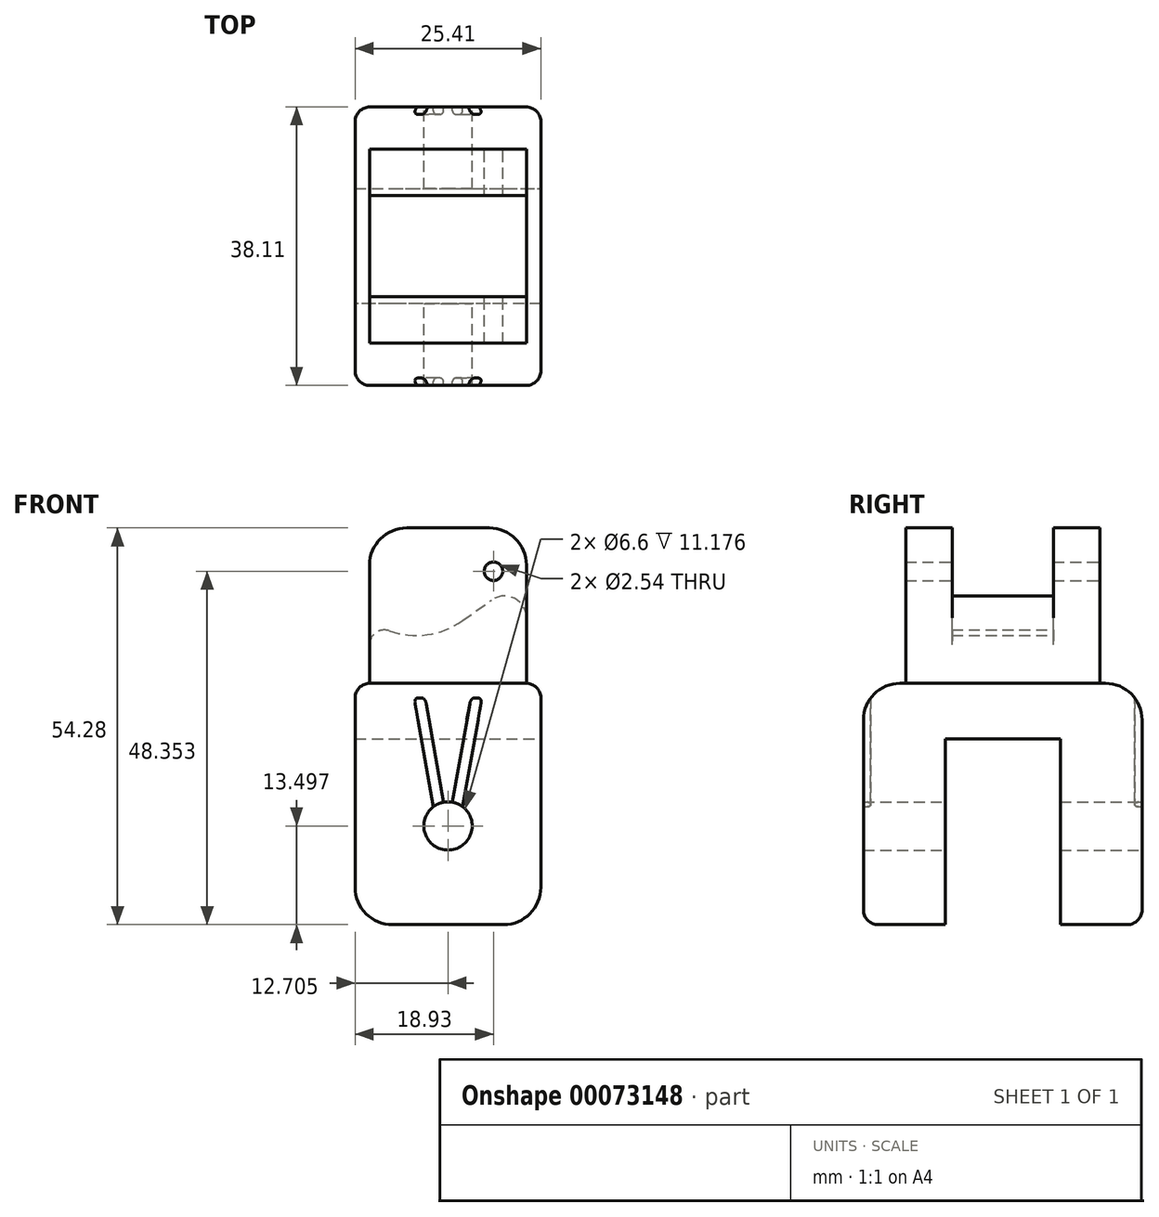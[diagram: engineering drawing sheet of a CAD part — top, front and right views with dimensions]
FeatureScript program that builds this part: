
annotation { "Feature Type Name" : "Feature", "Feature Type Description" : "" }
export const myFeature = defineFeature(function(context is Context, id is Id, definition is map)
    precondition{}
    {
        {
            var Q0;
            Q0=qCreatedBy(makeId("Front.planeOp"),FACE);
            var sketch = newSketch(context, id + "F0", { "sketchPlane" : qUnion([Q0])});
            skLineSegment(sketch, "E0.rect.bottom", {"start": v(6.35, -4.28) * mm, "end": v(-6.35, -4.28) * mm});
            skLineSegment(sketch, "E0.rect.left", {"start": v(6.35, -4.28) * mm, "end": v(6.35, 4.28) * mm});
            skLineSegment(sketch, "E0.rect.right", {"start": v(-6.35, -4.28) * mm, "end": v(-6.35, 4.28) * mm});
            skPoint(sketch, "E0.rect.middle", {"position": v(0, 0) * mm});
            skArc(sketch, "E1", {"start": v(-6.35, 4.28) * mm, "mid": v(0, 2.26) * mm, "end": v(6.35, 4.28) * mm});
            skLineSegment(sketch, "E2", {"start": v(6.35, 4.28) * mm, "end": v(15.1, 10.47) * mm});
            skLineSegment(sketch, "E3", {"start": v(15.1, 10.47) * mm, "end": v(15.1, -4.28) * mm});
            skLineSegment(sketch, "E4", {"start": v(15.1, -4.28) * mm, "end": v(6.35, -4.28) * mm});
            skSolve(sketch);
        }
        {
            var Q0;
            Q0=makeQuery(id+"F0.imprint","IMPRINT",FACE,{"disambiguationData":[TD([[makeQuery(id+"F0.imprint","IMPRINT",EDGE,{"derivedFrom":sQuery(id+"F0.wireOp",EDGE,"E0.rect.bottom")}),-1.0]])]});
            var Q1;
            Q1=makeQuery(id+"F0.imprint","IMPRINT",FACE,{"disambiguationData":[TD([[makeQuery(id+"F0.imprint","IMPRINT",EDGE,{"derivedFrom":sQuery(id+"F0.wireOp",EDGE,"E0.rect.left")}),-1.0]])]});
            extrude(context, id + "F1", {"entities" : qUnion([Q0, Q1]), "depth" : 13.85 * mm});
        }
        {
            var Q0;
            Q0=makeQuery(id+"F1.opExtrude","SWEPT_EDGE",EDGE,{"disambiguationData":[OSD([sQuery(id+"F0.wireOp",EDGE,"E0.rect.right"),sQuery(id+"F0.wireOp",EDGE,"E1")])]});
            fillet(context, id + "F2", {"entities" : qUnion([Q0]), "radius" : 2 * mm, "tangentPropagation" : true, "allowEdgeOverflow" : false});
        }
        {
            var Q0;
            Q0=makeQuery(id+"F1.opExtrude","CAP_FACE",FACE,{"disambiguationData":[OSD([sQuery(id+"F0.wireOp",EDGE,"E0.rect.bottom"),sQuery(id+"F0.wireOp",EDGE,"E0.rect.top"),sQuery(id+"F0.wireOp",EDGE,"E0.rect.left"),sQuery(id+"F0.wireOp",EDGE,"E0.rect.right")])],"isStart":false});
            var sketch = newSketch(context, id + "F3", { "sketchPlane" : qUnion([Q0])});
            skLineSegment(sketch, "E5.bottom", {"start": v(-6.35, -4.28) * mm, "end": v(15.1, -4.28) * mm});
            skLineSegment(sketch, "E5.top", {"start": v(-6.35, 16.98) * mm, "end": v(15.1, 16.98) * mm});
            skLineSegment(sketch, "E5.left", {"start": v(-6.35, -4.28) * mm, "end": v(-6.35, 16.98) * mm});
            skLineSegment(sketch, "E5.right", {"start": v(15.1, -4.28) * mm, "end": v(15.1, 16.98) * mm});
            skSolve(sketch);
        }
        {
            var Q0;
            Q0=qSketchRegion(id+"F3",true);
            extrude(context, id + "F4", {"entities" : qUnion([Q0]), "operationType" : NewBodyOperationType.ADD, "depth" : 6.35 * mm});
        }
        {
            var Q0;
            Q0=makeQuery(id+"F1.opExtrude","CAP_FACE",FACE,{"disambiguationData":[OSD([sQuery(id+"F0.wireOp",EDGE,"E0.rect.bottom"),sQuery(id+"F0.wireOp",EDGE,"E0.rect.top"),sQuery(id+"F0.wireOp",EDGE,"E0.rect.left"),sQuery(id+"F0.wireOp",EDGE,"E0.rect.right")])],"isStart":true});
            var sketch = newSketch(context, id + "F5", { "sketchPlane" : qUnion([Q0])});
            skLineSegment(sketch, "E6.bottom", {"start": v(6.35, -4.28) * mm, "end": v(-15.1, -4.28) * mm});
            skLineSegment(sketch, "E6.top", {"start": v(6.35, 16.98) * mm, "end": v(-15.1, 16.98) * mm});
            skLineSegment(sketch, "E6.left", {"start": v(6.35, -4.28) * mm, "end": v(6.35, 16.98) * mm});
            skLineSegment(sketch, "E6.right", {"start": v(-15.1, -4.28) * mm, "end": v(-15.1, 16.98) * mm});
            skSolve(sketch);
        }
        {
            var Q0;
            Q0=qSketchRegion(id+"F5",true);
            extrude(context, id + "F6", {"entities" : qUnion([Q0]), "operationType" : NewBodyOperationType.ADD, "depth" : 6.35 * mm});
        }
        {
            var Q0;
            Q0=makeQuery(id+"F6.opExtrude","CAP_FACE",FACE,{"disambiguationData":[OSD([sQuery(id+"F5.wireOp",EDGE,"E6.bottom"),sQuery(id+"F5.wireOp",EDGE,"E6.top"),sQuery(id+"F5.wireOp",EDGE,"E6.left"),sQuery(id+"F5.wireOp",EDGE,"E6.right")])],"isStart":false});
            var sketch = newSketch(context, id + "F7", { "sketchPlane" : qUnion([Q0])});
            skCircle(sketch, "E7", {"center": v(-10.6, 11.05) * mm, "radius": 1.27 * mm});
            skSolve(sketch);
        }
        {
            var Q0;
            Q0=qSketchRegion(id+"F7",true);
            extrude(context, id + "F8", {"entities" : qUnion([Q0]), "operationType" : NewBodyOperationType.REMOVE, "endBound" : BoundingType.THROUGH_ALL, "oppositeDirection" : true, "depth" : 25.4 * mm});
        }
        {
            var Q0;
            Q0=makeQuery(id+"F6.boolean.opBoolean","MERGE",FACE,{"derivedFrom":[makeQuery(id+"F4.boolean.opBoolean","MERGE",FACE,{"derivedFrom":[makeQuery(id+"F1.opExtrude","SWEPT_FACE",FACE,{"disambiguationData":[OSD([sQuery(id+"F0.wireOp",EDGE,"E0.rect.bottom")])]}),makeQuery(id+"F4.opExtrude","SWEPT_FACE",FACE,{"disambiguationData":[OSD([sQuery(id+"F3.wireOp",EDGE,"E5.bottom")])]})]}),makeQuery(id+"F6.opExtrude","SWEPT_FACE",FACE,{"disambiguationData":[OSD([sQuery(id+"F5.wireOp",EDGE,"E6.bottom")])]})]});
            var sketch = newSketch(context, id + "F9", { "sketchPlane" : qUnion([Q0])});
            skLineSegment(sketch, "E8", {"start": v(15.1, -6.35) * mm, "end": v(-6.35, 20.2) * mm});
            skLineSegment(sketch, "E9", {"start": v(-6.35, -6.35) * mm, "end": v(15.1, 20.2) * mm});
            skLineSegment(sketch, "E10.rect.bottom", {"start": v(17.07, 25.97) * mm, "end": v(-8.33, 25.97) * mm});
            skLineSegment(sketch, "E10.rect.top", {"start": v(17.07, -12.13) * mm, "end": v(-8.32, -12.13) * mm});
            skLineSegment(sketch, "E10.rect.left", {"start": v(17.07, 25.97) * mm, "end": v(17.07, -12.13) * mm});
            skLineSegment(sketch, "E10.rect.right", {"start": v(-8.33, 25.98) * mm, "end": v(-8.33, -12.13) * mm});
            skPoint(sketch, "E10.rect.middle", {"position": v(4.37, 6.92) * mm});
            skSolve(sketch);
        }
        {
            var Q0;
            Q0=qSketchRegion(id+"F9",true);
            extrude(context, id + "F10", {"entities" : qUnion([Q0]), "operationType" : NewBodyOperationType.ADD, "depth" : 7.62 * mm});
        }
        {
            var Q0;
            Q0=makeQuery(id+"F10.opExtrude","CAP_FACE",FACE,{"disambiguationData":[OSD([sQuery(id+"F9.wireOp",EDGE,"E10.rect.bottom"),sQuery(id+"F9.wireOp",EDGE,"E10.rect.top"),sQuery(id+"F9.wireOp",EDGE,"E10.rect.left"),sQuery(id+"F9.wireOp",EDGE,"E10.rect.right")])],"isStart":false});
            var sketch = newSketch(context, id + "F11", { "sketchPlane" : qUnion([Q0])});
            skLineSegment(sketch, "E11.top", {"start": v(17.07, 14.8) * mm, "end": v(-8.33, 14.8) * mm});
            skLineSegment(sketch, "E12", {"start": v(-8.33, -0.95) * mm, "end": v(17.07, -0.95) * mm});
            skSolve(sketch);
        }
        {
            var Q0;
            {var subQ0=sQuery(id+"F11.wireOp",EDGE,"E12");Q0=makeQuery(id+"F11.imprint","IMPRINT",FACE,{"disambiguationData":[TD([[makeQuery(id+"F11.imprint","IMPRINT",EDGE,{"derivedFrom":subQ0}),-1.0]])]});}
            var Q1;
            {var subQ5=makeQuery(id+"F10.opExtrude","CAP_EDGE",EDGE,{"disambiguationData":[OSD([sQuery(id+"F9.wireOp",EDGE,"E10.rect.bottom")])],"isStart":false});Q1=makeQuery(id+"F11.imprint","IMPRINT",FACE,{"disambiguationData":[TD([[makeQuery(id+"F11.imprint","IMPRINT",EDGE,{"derivedFrom":subQ5}),1.0]])]});}
            extrude(context, id + "F12", {"entities" : qUnion([Q0, Q1]), "operationType" : NewBodyOperationType.ADD, "depth" : 25.4 * mm});
        }
        {
            var Q0;
            {var subQ0=sQuery(id+"F9.wireOp",EDGE,"E10.rect.top");Q0=makeQuery(id+"F12.boolean.opBoolean","MERGE",FACE,{"derivedFrom":[makeQuery(id+"F10.opExtrude","SWEPT_FACE",FACE,{"disambiguationData":[OSD([subQ0])]}),makeQuery(id+"F12.opExtrude","SWEPT_FACE",FACE,{"disambiguationData":[OSD([subQ0])]})]});}
            var sketch = newSketch(context, id + "F13", { "sketchPlane" : qUnion([Q0])});
            skCircle(sketch, "E13", {"center": v(-4.38, -23.8) * mm, "radius": 3.3 * mm});
            skSolve(sketch);
        }
        {
            var Q0;
            Q0=qSketchRegion(id+"F13",true);
            extrude(context, id + "F14", {"entities" : qUnion([Q0]), "operationType" : NewBodyOperationType.REMOVE, "endBound" : BoundingType.THROUGH_ALL, "oppositeDirection" : true, "depth" : 25.4 * mm});
        }
        {
            var Q0;
            {var subQ0=sQuery(id+"F9.wireOp",EDGE,"E10.rect.right");var subQ1=makeQuery(id+"F10.opExtrude","CAP_EDGE",EDGE,{"disambiguationData":[OSD([subQ0])],"isStart":false});Q0=makeQuery(id+"F12.opExtrude","CAP_EDGE",EDGE,{"disambiguationData":[OSD([subQ0]),TDD([makeQuery(id+"F11.imprint","IMPRINT",EDGE,{"disambiguationData":[TD([[makeQuery(id+"F11.imprint","INTERSECT",VERTEX,{"derivedFrom":[makeQuery(id+"F10.opExtrude","CAP_EDGE",EDGE,{"disambiguationData":[OSD([sQuery(id+"F9.wireOp",EDGE,"E10.rect.top")])],"isStart":false}),subQ1]}),1.0]])],"derivedFrom":subQ1})])],"isStart":false});}
            var Q1;
            {var subQ0=sQuery(id+"F9.wireOp",EDGE,"E10.rect.left");var subQ1=makeQuery(id+"F10.opExtrude","CAP_EDGE",EDGE,{"disambiguationData":[OSD([subQ0])],"isStart":false});Q1=makeQuery(id+"F12.opExtrude","CAP_EDGE",EDGE,{"disambiguationData":[OSD([subQ0]),TDD([makeQuery(id+"F11.imprint","IMPRINT",EDGE,{"disambiguationData":[TD([[makeQuery(id+"F11.imprint","INTERSECT",VERTEX,{"derivedFrom":[makeQuery(id+"F10.opExtrude","CAP_EDGE",EDGE,{"disambiguationData":[OSD([sQuery(id+"F9.wireOp",EDGE,"E10.rect.top")])],"isStart":false}),subQ1]}),1.0]])],"derivedFrom":subQ1})])],"isStart":false});}
            var Q2;
            {var subQ0=sQuery(id+"F9.wireOp",EDGE,"E10.rect.right");var subQ1=makeQuery(id+"F10.opExtrude","CAP_EDGE",EDGE,{"disambiguationData":[OSD([subQ0])],"isStart":false});Q2=makeQuery(id+"F12.opExtrude","CAP_EDGE",EDGE,{"disambiguationData":[OSD([subQ0]),TDD([makeQuery(id+"F11.imprint","IMPRINT",EDGE,{"disambiguationData":[TD([[makeQuery(id+"F11.imprint","INTERSECT",VERTEX,{"derivedFrom":[makeQuery(id+"F10.opExtrude","CAP_EDGE",EDGE,{"disambiguationData":[OSD([sQuery(id+"F9.wireOp",EDGE,"E10.rect.bottom")])],"isStart":false}),subQ1]}),-1.0]])],"derivedFrom":subQ1})])],"isStart":false});}
            var Q3;
            {var subQ0=sQuery(id+"F9.wireOp",EDGE,"E10.rect.left");var subQ1=makeQuery(id+"F10.opExtrude","CAP_EDGE",EDGE,{"disambiguationData":[OSD([subQ0])],"isStart":false});Q3=makeQuery(id+"F12.opExtrude","CAP_EDGE",EDGE,{"disambiguationData":[OSD([subQ0]),TDD([makeQuery(id+"F11.imprint","IMPRINT",EDGE,{"disambiguationData":[TD([[makeQuery(id+"F11.imprint","INTERSECT",VERTEX,{"derivedFrom":[makeQuery(id+"F10.opExtrude","CAP_EDGE",EDGE,{"disambiguationData":[OSD([sQuery(id+"F9.wireOp",EDGE,"E10.rect.bottom")])],"isStart":false}),subQ1]}),-1.0]])],"derivedFrom":subQ1})])],"isStart":false});}
            var Q4;
            Q4=makeQuery(id+"F12.opExtrude","CAP_EDGE",EDGE,{"disambiguationData":[OSD([sQuery(id+"F11.wireOp",EDGE,"E11.top")])],"isStart":true});
            var Q5;
            Q5=makeQuery(id+"F12.opExtrude","CAP_EDGE",EDGE,{"disambiguationData":[OSD([sQuery(id+"F11.wireOp",EDGE,"E12")])],"isStart":true});
            var Q6;
            Q6=makeQuery(id+"F6.boolean.opBoolean","MERGE",EDGE,{"derivedFrom":[makeQuery(id+"F4.boolean.opBoolean","MERGE",EDGE,{"derivedFrom":[makeQuery(id+"F1.opExtrude","SWEPT_EDGE",EDGE,{"disambiguationData":[OSD([sQuery(id+"F0.wireOp",EDGE,"E0.rect.bottom"),sQuery(id+"F0.wireOp",EDGE,"E0.rect.right")])]}),makeQuery(id+"F4.opExtrude","SWEPT_EDGE",EDGE,{"disambiguationData":[OSD([sQuery(id+"F3.wireOp",EDGE,"E5.bottom"),sQuery(id+"F3.wireOp",EDGE,"E5.left")])]})]}),makeQuery(id+"F6.opExtrude","SWEPT_EDGE",EDGE,{"disambiguationData":[OSD([sQuery(id+"F5.wireOp",EDGE,"E6.bottom"),sQuery(id+"F5.wireOp",EDGE,"E6.left")])]})]});
            var Q7;
            Q7=makeQuery(id+"F4.opExtrude","CAP_EDGE",EDGE,{"disambiguationData":[OSD([sQuery(id+"F3.wireOp",EDGE,"E5.bottom")])],"isStart":false});
            var Q8;
            Q8=makeQuery(id+"F6.boolean.opBoolean","MERGE",EDGE,{"derivedFrom":[makeQuery(id+"F4.boolean.opBoolean","MERGE",EDGE,{"derivedFrom":[makeQuery(id+"F1.opExtrude","SWEPT_EDGE",EDGE,{"disambiguationData":[OSD([sQuery(id+"F0.wireOp",EDGE,"E3"),sQuery(id+"F0.wireOp",EDGE,"E4")])]}),makeQuery(id+"F4.opExtrude","SWEPT_EDGE",EDGE,{"disambiguationData":[OSD([sQuery(id+"F3.wireOp",EDGE,"E5.bottom"),sQuery(id+"F3.wireOp",EDGE,"E5.right")])]})]}),makeQuery(id+"F6.opExtrude","SWEPT_EDGE",EDGE,{"disambiguationData":[OSD([sQuery(id+"F5.wireOp",EDGE,"E6.bottom"),sQuery(id+"F5.wireOp",EDGE,"E6.right")])]})]});
            var Q9;
            Q9=makeQuery(id+"F6.opExtrude","CAP_EDGE",EDGE,{"disambiguationData":[OSD([sQuery(id+"F5.wireOp",EDGE,"E6.bottom")])],"isStart":false});
            var Q10;
            Q10=makeQuery(id+"F6.opExtrude","SWEPT_EDGE",EDGE,{"disambiguationData":[OSD([sQuery(id+"F5.wireOp",EDGE,"E6.top"),sQuery(id+"F5.wireOp",EDGE,"E6.right")])]});
            var Q11;
            Q11=makeQuery(id+"F6.opExtrude","SWEPT_EDGE",EDGE,{"disambiguationData":[OSD([sQuery(id+"F5.wireOp",EDGE,"E6.top"),sQuery(id+"F5.wireOp",EDGE,"E6.left")])]});
            var Q12;
            Q12=makeQuery(id+"F4.opExtrude","SWEPT_EDGE",EDGE,{"disambiguationData":[OSD([sQuery(id+"F3.wireOp",EDGE,"E5.top"),sQuery(id+"F3.wireOp",EDGE,"E5.right")])]});
            var Q13;
            Q13=makeQuery(id+"F4.opExtrude","SWEPT_EDGE",EDGE,{"disambiguationData":[OSD([sQuery(id+"F3.wireOp",EDGE,"E5.top"),sQuery(id+"F3.wireOp",EDGE,"E5.left")])]});
            fillet(context, id + "F15", {"entities" : qUnion([Q0, Q1, Q2, Q3, Q4, Q5, Q6, Q7, Q8, Q9, Q10, Q11, Q12, Q13]), "radius" : 5.08 * mm, "tangentPropagation" : true, "allowEdgeOverflow" : false});
        }
        {
            var Q0;
            Q0=makeQuery(id+"F10.opExtrude","CAP_EDGE",EDGE,{"disambiguationData":[OSD([sQuery(id+"F9.wireOp",EDGE,"E10.rect.top")])],"isStart":true});
            var Q1;
            Q1=makeQuery(id+"F10.opExtrude","CAP_EDGE",EDGE,{"disambiguationData":[OSD([sQuery(id+"F9.wireOp",EDGE,"E10.rect.bottom")])],"isStart":true});
            var Q2;
            {var subQ0=sQuery(id+"F9.wireOp",EDGE,"E10.rect.right");var subQ1=makeQuery(id+"F10.opExtrude","CAP_EDGE",EDGE,{"disambiguationData":[OSD([subQ0])],"isStart":false});Q2=makeQuery(id+"F15.opFillet","BLEND_EDGE",EDGE,{"blendedFrom":[makeQuery(id+"F6.boolean.opBoolean","MERGE",EDGE,{"derivedFrom":[makeQuery(id+"F4.boolean.opBoolean","MERGE",EDGE,{"derivedFrom":[makeQuery(id+"F1.opExtrude","SWEPT_EDGE",EDGE,{"disambiguationData":[OSD([sQuery(id+"F0.wireOp",EDGE,"E0.rect.bottom"),sQuery(id+"F0.wireOp",EDGE,"E0.rect.right")])]}),makeQuery(id+"F4.opExtrude","SWEPT_EDGE",EDGE,{"disambiguationData":[OSD([sQuery(id+"F3.wireOp",EDGE,"E5.bottom"),sQuery(id+"F3.wireOp",EDGE,"E5.left")])]})]}),makeQuery(id+"F6.opExtrude","SWEPT_EDGE",EDGE,{"disambiguationData":[OSD([sQuery(id+"F5.wireOp",EDGE,"E6.bottom"),sQuery(id+"F5.wireOp",EDGE,"E6.left")])]})]}),makeQuery(id+"F12.boolean.opBoolean","MERGE",FACE,{"derivedFrom":[makeQuery(id+"F10.opExtrude","SWEPT_FACE",FACE,{"disambiguationData":[OSD([subQ0])]}),makeQuery(id+"F12.opExtrude","SWEPT_FACE",FACE,{"disambiguationData":[OSD([subQ0]),TDD([makeQuery(id+"F11.imprint","IMPRINT",EDGE,{"disambiguationData":[TD([[makeQuery(id+"F11.imprint","INTERSECT",VERTEX,{"derivedFrom":[makeQuery(id+"F10.opExtrude","CAP_EDGE",EDGE,{"disambiguationData":[OSD([sQuery(id+"F9.wireOp",EDGE,"E10.rect.bottom")])],"isStart":false}),subQ1]}),-1.0]])],"derivedFrom":subQ1})])]}),makeQuery(id+"F12.opExtrude","SWEPT_FACE",FACE,{"disambiguationData":[OSD([subQ0]),TDD([makeQuery(id+"F11.imprint","IMPRINT",EDGE,{"disambiguationData":[TD([[makeQuery(id+"F11.imprint","INTERSECT",VERTEX,{"derivedFrom":[makeQuery(id+"F10.opExtrude","CAP_EDGE",EDGE,{"disambiguationData":[OSD([sQuery(id+"F9.wireOp",EDGE,"E10.rect.top")])],"isStart":false}),subQ1]}),1.0]])],"derivedFrom":subQ1})])]})]})],"blendedInto":[makeQuery(id+"F12.boolean.opBoolean","MERGE",FACE,{"derivedFrom":[makeQuery(id+"F10.opExtrude","SWEPT_FACE",FACE,{"disambiguationData":[OSD([subQ0])]}),makeQuery(id+"F12.opExtrude","SWEPT_FACE",FACE,{"disambiguationData":[OSD([subQ0]),TDD([makeQuery(id+"F11.imprint","IMPRINT",EDGE,{"disambiguationData":[TD([[makeQuery(id+"F11.imprint","INTERSECT",VERTEX,{"derivedFrom":[makeQuery(id+"F10.opExtrude","CAP_EDGE",EDGE,{"disambiguationData":[OSD([sQuery(id+"F9.wireOp",EDGE,"E10.rect.bottom")])],"isStart":false}),subQ1]}),-1.0]])],"derivedFrom":subQ1})])]}),makeQuery(id+"F12.opExtrude","SWEPT_FACE",FACE,{"disambiguationData":[OSD([subQ0]),TDD([makeQuery(id+"F11.imprint","IMPRINT",EDGE,{"disambiguationData":[TD([[makeQuery(id+"F11.imprint","INTERSECT",VERTEX,{"derivedFrom":[makeQuery(id+"F10.opExtrude","CAP_EDGE",EDGE,{"disambiguationData":[OSD([sQuery(id+"F9.wireOp",EDGE,"E10.rect.top")])],"isStart":false}),subQ1]}),1.0]])],"derivedFrom":subQ1})])]})]})]});}
            var Q3;
            {var subQ0=sQuery(id+"F9.wireOp",EDGE,"E10.rect.left");var subQ1=makeQuery(id+"F10.opExtrude","CAP_EDGE",EDGE,{"disambiguationData":[OSD([subQ0])],"isStart":false});Q3=makeQuery(id+"F15.opFillet","BLEND_EDGE",EDGE,{"blendedFrom":[makeQuery(id+"F6.boolean.opBoolean","MERGE",EDGE,{"derivedFrom":[makeQuery(id+"F4.boolean.opBoolean","MERGE",EDGE,{"derivedFrom":[makeQuery(id+"F1.opExtrude","SWEPT_EDGE",EDGE,{"disambiguationData":[OSD([sQuery(id+"F0.wireOp",EDGE,"E3"),sQuery(id+"F0.wireOp",EDGE,"E4")])]}),makeQuery(id+"F4.opExtrude","SWEPT_EDGE",EDGE,{"disambiguationData":[OSD([sQuery(id+"F3.wireOp",EDGE,"E5.bottom"),sQuery(id+"F3.wireOp",EDGE,"E5.right")])]})]}),makeQuery(id+"F6.opExtrude","SWEPT_EDGE",EDGE,{"disambiguationData":[OSD([sQuery(id+"F5.wireOp",EDGE,"E6.bottom"),sQuery(id+"F5.wireOp",EDGE,"E6.right")])]})]}),makeQuery(id+"F12.boolean.opBoolean","MERGE",FACE,{"derivedFrom":[makeQuery(id+"F10.opExtrude","SWEPT_FACE",FACE,{"disambiguationData":[OSD([subQ0])]}),makeQuery(id+"F12.opExtrude","SWEPT_FACE",FACE,{"disambiguationData":[OSD([subQ0]),TDD([makeQuery(id+"F11.imprint","IMPRINT",EDGE,{"disambiguationData":[TD([[makeQuery(id+"F11.imprint","INTERSECT",VERTEX,{"derivedFrom":[makeQuery(id+"F10.opExtrude","CAP_EDGE",EDGE,{"disambiguationData":[OSD([sQuery(id+"F9.wireOp",EDGE,"E10.rect.bottom")])],"isStart":false}),subQ1]}),-1.0]])],"derivedFrom":subQ1})])]}),makeQuery(id+"F12.opExtrude","SWEPT_FACE",FACE,{"disambiguationData":[OSD([subQ0]),TDD([makeQuery(id+"F11.imprint","IMPRINT",EDGE,{"disambiguationData":[TD([[makeQuery(id+"F11.imprint","INTERSECT",VERTEX,{"derivedFrom":[makeQuery(id+"F10.opExtrude","CAP_EDGE",EDGE,{"disambiguationData":[OSD([sQuery(id+"F9.wireOp",EDGE,"E10.rect.top")])],"isStart":false}),subQ1]}),1.0]])],"derivedFrom":subQ1})])]})]})],"blendedInto":[makeQuery(id+"F12.boolean.opBoolean","MERGE",FACE,{"derivedFrom":[makeQuery(id+"F10.opExtrude","SWEPT_FACE",FACE,{"disambiguationData":[OSD([subQ0])]}),makeQuery(id+"F12.opExtrude","SWEPT_FACE",FACE,{"disambiguationData":[OSD([subQ0]),TDD([makeQuery(id+"F11.imprint","IMPRINT",EDGE,{"disambiguationData":[TD([[makeQuery(id+"F11.imprint","INTERSECT",VERTEX,{"derivedFrom":[makeQuery(id+"F10.opExtrude","CAP_EDGE",EDGE,{"disambiguationData":[OSD([sQuery(id+"F9.wireOp",EDGE,"E10.rect.bottom")])],"isStart":false}),subQ1]}),-1.0]])],"derivedFrom":subQ1})])]}),makeQuery(id+"F12.opExtrude","SWEPT_FACE",FACE,{"disambiguationData":[OSD([subQ0]),TDD([makeQuery(id+"F11.imprint","IMPRINT",EDGE,{"disambiguationData":[TD([[makeQuery(id+"F11.imprint","INTERSECT",VERTEX,{"derivedFrom":[makeQuery(id+"F10.opExtrude","CAP_EDGE",EDGE,{"disambiguationData":[OSD([sQuery(id+"F9.wireOp",EDGE,"E10.rect.top")])],"isStart":false}),subQ1]}),1.0]])],"derivedFrom":subQ1})])]})]})]});}
            fillet(context, id + "F16", {"entities" : qUnion([Q0, Q1, Q2, Q3]), "radius" : 5 * mm, "tangentPropagation" : true, "allowEdgeOverflow" : false});
        }
        {
            var Q0;
            Q0=makeQuery(id+"F1.opExtrude","SWEPT_EDGE",EDGE,{"disambiguationData":[OSD([sQuery(id+"F0.wireOp",EDGE,"E2"),sQuery(id+"F0.wireOp",EDGE,"E3")])]});
            fillet(context, id + "F17", {"entities" : qUnion([Q0]), "radius" : 3 * mm, "tangentPropagation" : true, "allowEdgeOverflow" : false});
        }
        {
            var Q0;
            {var subQ0=sQuery(id+"F9.wireOp",EDGE,"E10.rect.right");var subQ1=makeQuery(id+"F10.opExtrude","CAP_EDGE",EDGE,{"disambiguationData":[OSD([subQ0])],"isStart":false});var subQ2=sQuery(id+"F9.wireOp",EDGE,"E10.rect.bottom");Q0=makeQuery(id+"F16.opFillet","BLEND_EDGE",EDGE,{"blendedFrom":[makeQuery(id+"F10.opExtrude","CAP_EDGE",EDGE,{"disambiguationData":[OSD([subQ2])],"isStart":true}),makeQuery(id+"F15.opFillet","BLEND_EDGE",EDGE,{"blendedFrom":[makeQuery(id+"F6.boolean.opBoolean","MERGE",EDGE,{"derivedFrom":[makeQuery(id+"F4.boolean.opBoolean","MERGE",EDGE,{"derivedFrom":[makeQuery(id+"F1.opExtrude","SWEPT_EDGE",EDGE,{"disambiguationData":[OSD([sQuery(id+"F0.wireOp",EDGE,"E0.rect.bottom"),sQuery(id+"F0.wireOp",EDGE,"E0.rect.right")])]}),makeQuery(id+"F4.opExtrude","SWEPT_EDGE",EDGE,{"disambiguationData":[OSD([sQuery(id+"F3.wireOp",EDGE,"E5.bottom"),sQuery(id+"F3.wireOp",EDGE,"E5.left")])]})]}),makeQuery(id+"F6.opExtrude","SWEPT_EDGE",EDGE,{"disambiguationData":[OSD([sQuery(id+"F5.wireOp",EDGE,"E6.bottom"),sQuery(id+"F5.wireOp",EDGE,"E6.left")])]})]}),makeQuery(id+"F12.boolean.opBoolean","MERGE",FACE,{"derivedFrom":[makeQuery(id+"F10.opExtrude","SWEPT_FACE",FACE,{"disambiguationData":[OSD([subQ0])]}),makeQuery(id+"F12.opExtrude","SWEPT_FACE",FACE,{"disambiguationData":[OSD([subQ0]),TDD([makeQuery(id+"F11.imprint","IMPRINT",EDGE,{"disambiguationData":[TD([[makeQuery(id+"F11.imprint","INTERSECT",VERTEX,{"derivedFrom":[makeQuery(id+"F10.opExtrude","CAP_EDGE",EDGE,{"disambiguationData":[OSD([subQ2])],"isStart":false}),subQ1]}),-1.0]])],"derivedFrom":subQ1})])]}),makeQuery(id+"F12.opExtrude","SWEPT_FACE",FACE,{"disambiguationData":[OSD([subQ0]),TDD([makeQuery(id+"F11.imprint","IMPRINT",EDGE,{"disambiguationData":[TD([[makeQuery(id+"F11.imprint","INTERSECT",VERTEX,{"derivedFrom":[makeQuery(id+"F10.opExtrude","CAP_EDGE",EDGE,{"disambiguationData":[OSD([sQuery(id+"F9.wireOp",EDGE,"E10.rect.top")])],"isStart":false}),subQ1]}),1.0]])],"derivedFrom":subQ1})])]})]})],"blendedInto":[makeQuery(id+"F12.boolean.opBoolean","MERGE",FACE,{"derivedFrom":[makeQuery(id+"F10.opExtrude","SWEPT_FACE",FACE,{"disambiguationData":[OSD([subQ0])]}),makeQuery(id+"F12.opExtrude","SWEPT_FACE",FACE,{"disambiguationData":[OSD([subQ0]),TDD([makeQuery(id+"F11.imprint","IMPRINT",EDGE,{"disambiguationData":[TD([[makeQuery(id+"F11.imprint","INTERSECT",VERTEX,{"derivedFrom":[makeQuery(id+"F10.opExtrude","CAP_EDGE",EDGE,{"disambiguationData":[OSD([subQ2])],"isStart":false}),subQ1]}),-1.0]])],"derivedFrom":subQ1})])]}),makeQuery(id+"F12.opExtrude","SWEPT_FACE",FACE,{"disambiguationData":[OSD([subQ0]),TDD([makeQuery(id+"F11.imprint","IMPRINT",EDGE,{"disambiguationData":[TD([[makeQuery(id+"F11.imprint","INTERSECT",VERTEX,{"derivedFrom":[makeQuery(id+"F10.opExtrude","CAP_EDGE",EDGE,{"disambiguationData":[OSD([sQuery(id+"F9.wireOp",EDGE,"E10.rect.top")])],"isStart":false}),subQ1]}),1.0]])],"derivedFrom":subQ1})])]})]})]})],"blendedInto":[]});}
            var Q1;
            {var subQ0=sQuery(id+"F9.wireOp",EDGE,"E10.rect.right");var subQ1=sQuery(id+"F9.wireOp",EDGE,"E10.rect.top");Q1=makeQuery(id+"F12.boolean.opBoolean","MERGE",EDGE,{"derivedFrom":[makeQuery(id+"F10.opExtrude","SWEPT_EDGE",EDGE,{"disambiguationData":[OSD([subQ1,subQ0])]}),makeQuery(id+"F12.opExtrude","SWEPT_EDGE",EDGE,{"disambiguationData":[OSD([subQ1,subQ0])]})]});}
            fillet(context, id + "F18", {"entities" : qUnion([Q0, Q1]), "radius" : 2 * mm, "tangentPropagation" : true, "allowEdgeOverflow" : false});
        }
        {
            var Q0;
            {var subQ0=sQuery(id+"F9.wireOp",EDGE,"E10.rect.bottom");Q0=makeQuery(id+"F12.boolean.opBoolean","MERGE",FACE,{"derivedFrom":[makeQuery(id+"F10.opExtrude","SWEPT_FACE",FACE,{"disambiguationData":[OSD([subQ0])]}),makeQuery(id+"F12.opExtrude","SWEPT_FACE",FACE,{"disambiguationData":[OSD([subQ0])]})]});}
            var sketch = newSketch(context, id + "F19", { "sketchPlane" : qUnion([Q0])});
            skLineSegment(sketch, "E14", {"start": v(4.38, -23.96) * mm, "end": v(4.38, -9.25) * mm});
            skLineSegment(sketch, "E15", {"start": v(6.97, -9.25) * mm, "end": v(4.38, -23.96) * mm});
            skLineSegment(sketch, "E16", {"start": v(4.38, -23.96) * mm, "end": v(1.78, -9.25) * mm});
            skLineSegment(sketch, "E17", {"start": v(0.26, -9.25) * mm, "end": v(2.84, -23.9) * mm});
            skLineSegment(sketch, "E18", {"start": v(2.84, -23.9) * mm, "end": v(4.38, -23.96) * mm});
            skLineSegment(sketch, "E19", {"start": v(8.5, -9.25) * mm, "end": v(5.9, -23.96) * mm});
            skLineSegment(sketch, "E20", {"start": v(5.9, -23.96) * mm, "end": v(4.38, -23.96) * mm});
            skLineSegment(sketch, "E21", {"start": v(0.26, -9.25) * mm, "end": v(-0.57, -4.54) * mm});
            skLineSegment(sketch, "E22", {"start": v(1.78, -9.25) * mm, "end": v(0.95, -4.54) * mm});
            skLineSegment(sketch, "E23", {"start": v(0.95, -4.54) * mm, "end": v(-0.57, -4.54) * mm});
            skLineSegment(sketch, "E24", {"start": v(6.97, -9.25) * mm, "end": v(7.8, -4.54) * mm});
            skLineSegment(sketch, "E25", {"start": v(8.5, -9.25) * mm, "end": v(9.32, -4.54) * mm});
            skLineSegment(sketch, "E26", {"start": v(9.32, -4.54) * mm, "end": v(7.8, -4.54) * mm});
            skSolve(sketch);
        }
        {
            var Q0;
            Q0 = qSketchRegion(id + "F19", true);
            extrude(context, id + "F20", {"entities" : qUnion([Q0]), "operationType" : NewBodyOperationType.REMOVE, "oppositeDirection" : true, "depth" : 1 * mm});
        }
        {
            var Q0;
            {var subQ0=sQuery(id+"F9.wireOp",EDGE,"E10.rect.top");Q0=makeQuery(id+"F12.boolean.opBoolean","MERGE",FACE,{"derivedFrom":[makeQuery(id+"F10.opExtrude","SWEPT_FACE",FACE,{"disambiguationData":[OSD([subQ0])]}),makeQuery(id+"F12.opExtrude","SWEPT_FACE",FACE,{"disambiguationData":[OSD([subQ0])]})]});}
            var sketch = newSketch(context, id + "F21", { "sketchPlane" : qUnion([Q0])});
            skLineSegment(sketch, "E27", {"start": v(-4.37, -23.96) * mm, "end": v(-4.37, -9.25) * mm});
            skLineSegment(sketch, "E28", {"start": v(-1.78, -9.25) * mm, "end": v(-4.37, -23.96) * mm});
            skLineSegment(sketch, "E29", {"start": v(-4.37, -23.96) * mm, "end": v(-6.97, -9.25) * mm});
            skLineSegment(sketch, "E30", {"start": v(-8.5, -9.25) * mm, "end": v(-5.9, -23.9) * mm});
            skLineSegment(sketch, "E31", {"start": v(-5.9, -23.9) * mm, "end": v(-4.37, -23.96) * mm});
            skLineSegment(sketch, "E32", {"start": v(-0.26, -9.25) * mm, "end": v(-2.85, -23.96) * mm});
            skLineSegment(sketch, "E33", {"start": v(-2.85, -23.96) * mm, "end": v(-4.37, -23.96) * mm});
            skLineSegment(sketch, "E34", {"start": v(-8.5, -9.25) * mm, "end": v(-9.32, -4.54) * mm});
            skLineSegment(sketch, "E35", {"start": v(-6.97, -9.25) * mm, "end": v(-7.8, -4.54) * mm});
            skLineSegment(sketch, "E36", {"start": v(-7.8, -4.54) * mm, "end": v(-9.32, -4.54) * mm});
            skLineSegment(sketch, "E37", {"start": v(-1.78, -9.25) * mm, "end": v(-0.95, -4.54) * mm});
            skLineSegment(sketch, "E38", {"start": v(-0.26, -9.25) * mm, "end": v(0.57, -4.54) * mm});
            skLineSegment(sketch, "E39", {"start": v(0.57, -4.54) * mm, "end": v(-0.95, -4.54) * mm});
            skSolve(sketch);
        }
        {
            var Q0;
            Q0 = qSketchRegion(id + "F21", true);
            extrude(context, id + "F22", {"entities" : qUnion([Q0]), "operationType" : NewBodyOperationType.REMOVE, "oppositeDirection" : true, "depth" : 1 * mm});
        }
        {
            var Q0;
            Q0=makeQuery(id+"F22.boolean.opBoolean","COPY",EDGE,{"derivedFrom":makeQuery(id+"F22.opExtrude","CAP_EDGE",EDGE,{"disambiguationData":[OSD([sQuery(id+"F21.wireOp",EDGE,"E30"),sQuery(id+"F21.wireOp",EDGE,"E34")])],"isStart":false})});
            var Q1;
            Q1=makeQuery(id+"F22.boolean.opBoolean","COPY",EDGE,{"derivedFrom":makeQuery(id+"F22.opExtrude","CAP_EDGE",EDGE,{"disambiguationData":[OSD([sQuery(id+"F21.wireOp",EDGE,"E32"),sQuery(id+"F21.wireOp",EDGE,"E38")])],"isStart":false})});
            var Q2;
            Q2=makeQuery(id+"F22.boolean.opBoolean","COPY",EDGE,{"derivedFrom":makeQuery(id+"F22.opExtrude","CAP_EDGE",EDGE,{"disambiguationData":[OSD([sQuery(id+"F21.wireOp",EDGE,"E29"),sQuery(id+"F21.wireOp",EDGE,"E35")])],"isStart":false})});
            var Q3;
            Q3=makeQuery(id+"F22.boolean.opBoolean","COPY",EDGE,{"derivedFrom":makeQuery(id+"F22.opExtrude","CAP_EDGE",EDGE,{"disambiguationData":[OSD([sQuery(id+"F21.wireOp",EDGE,"E28"),sQuery(id+"F21.wireOp",EDGE,"E37")])],"isStart":false})});
            var Q4;
            Q4=makeQuery(id+"F20.boolean.opBoolean","COPY",EDGE,{"derivedFrom":makeQuery(id+"F20.opExtrude","CAP_EDGE",EDGE,{"disambiguationData":[OSD([sQuery(id+"F19.wireOp",EDGE,"E17"),sQuery(id+"F19.wireOp",EDGE,"E21")])],"isStart":false})});
            var Q5;
            Q5=makeQuery(id+"F20.boolean.opBoolean","COPY",EDGE,{"derivedFrom":makeQuery(id+"F20.opExtrude","CAP_EDGE",EDGE,{"disambiguationData":[OSD([sQuery(id+"F19.wireOp",EDGE,"E15"),sQuery(id+"F19.wireOp",EDGE,"E24")])],"isStart":false})});
            var Q6;
            Q6=makeQuery(id+"F20.boolean.opBoolean","COPY",EDGE,{"derivedFrom":makeQuery(id+"F20.opExtrude","CAP_EDGE",EDGE,{"disambiguationData":[OSD([sQuery(id+"F19.wireOp",EDGE,"E16"),sQuery(id+"F19.wireOp",EDGE,"E22")])],"isStart":false})});
            var Q7;
            Q7=makeQuery(id+"F20.boolean.opBoolean","COPY",EDGE,{"derivedFrom":makeQuery(id+"F20.opExtrude","CAP_EDGE",EDGE,{"disambiguationData":[OSD([sQuery(id+"F19.wireOp",EDGE,"E19"),sQuery(id+"F19.wireOp",EDGE,"E25")])],"isStart":false})});
            fillet(context, id + "F23", {"entities" : qUnion([Q0, Q1, Q2, Q3, Q4, Q5, Q6, Q7]), "radius" : .5 * mm, "tangentPropagation" : true, "allowEdgeOverflow" : false});
        }
    });
